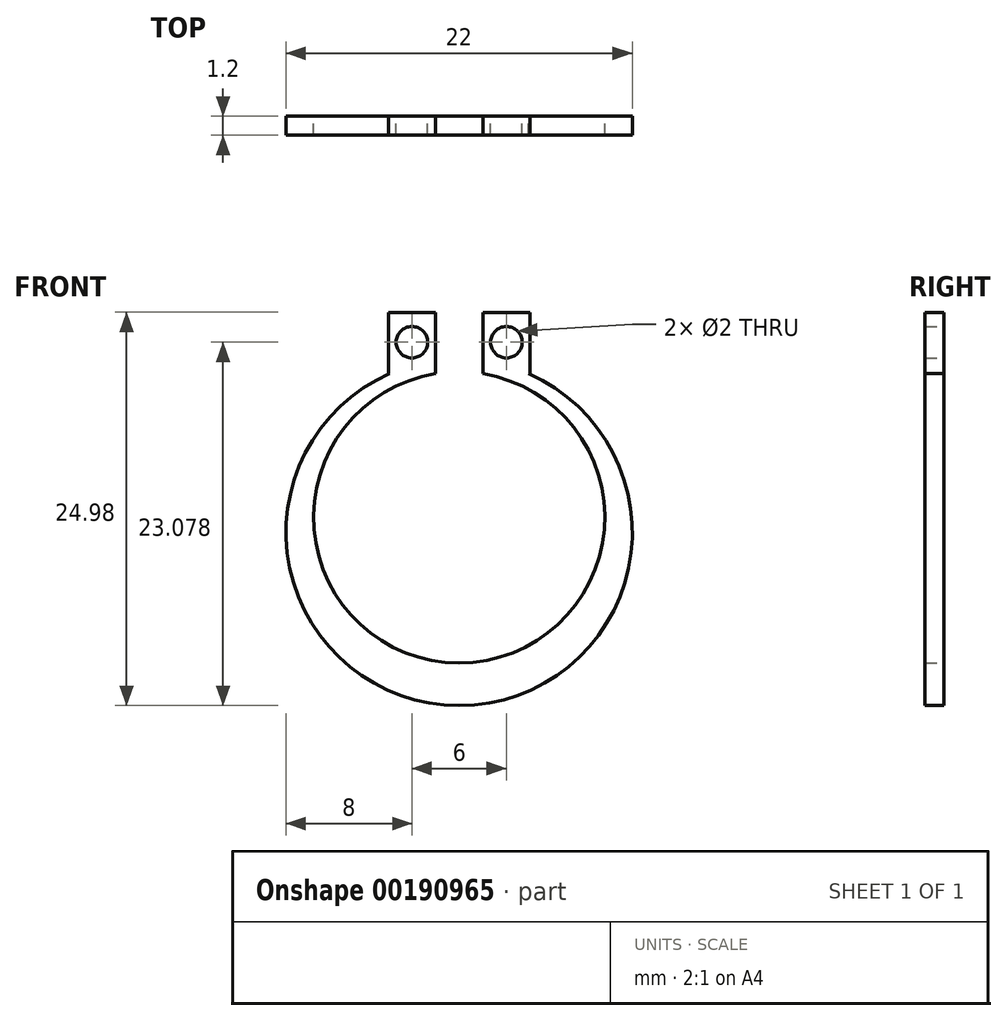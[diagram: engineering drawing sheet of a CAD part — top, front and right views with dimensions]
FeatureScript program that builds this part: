
annotation { "Feature Type Name" : "Feature", "Feature Type Description" : "" }
export const myFeature = defineFeature(function(context is Context, id is Id, definition is map)
    precondition{}
    {
        {
            var Q0;
            Q0=qCreatedBy(makeId("Front.planeOp"),FACE);
            var sketch = newSketch(context, id + "F0", { "sketchPlane" : qUnion([Q0])});
            skCircle(sketch, "E0", {"center": v(0, 0) * mm, "radius": 9.25 * mm});
            skCircle(sketch, "E1", {"center": v(0, -0.95) * mm, "radius": 11 * mm});
            skLineSegment(sketch, "E2.bottom", {"start": v(1.5, 9.13) * mm, "end": v(4.5, 9.13) * mm});
            skLineSegment(sketch, "E2.top", {"start": v(1.5, 13.03) * mm, "end": v(4.5, 13.03) * mm});
            skLineSegment(sketch, "E2.left", {"start": v(1.5, 9.13) * mm, "end": v(1.5, 13.03) * mm});
            skLineSegment(sketch, "E2.right", {"start": v(4.5, 9.13) * mm, "end": v(4.5, 13.03) * mm});
            skLineSegment(sketch, "E3.bottom", {"start": v(-1.5, 9.13) * mm, "end": v(-4.5, 9.13) * mm});
            skLineSegment(sketch, "E3.top", {"start": v(-1.5, 13.03) * mm, "end": v(-4.5, 13.03) * mm});
            skLineSegment(sketch, "E3.left", {"start": v(-1.5, 9.13) * mm, "end": v(-1.5, 13.03) * mm});
            skLineSegment(sketch, "E3.right", {"start": v(-4.5, 9.13) * mm, "end": v(-4.5, 13.03) * mm});
            skCircle(sketch, "E4", {"center": v(-3, 11.13) * mm, "radius": 1 * mm});
            skCircle(sketch, "E5", {"center": v(3, 11.13) * mm, "radius": 1 * mm});
            skSolve(sketch);
        }
        {
            var Q0;
            {var subQ0=sQuery(id+"F0.wireOp",EDGE,"E2.bottom");var subQ5=sQuery(id+"F0.wireOp",EDGE,"E1");var subQ6=makeQuery(id+"F0.imprint","INTERSECT",VERTEX,{"derivedFrom":[subQ5,subQ0]});Q0=makeQuery(id+"F0.imprint","IMPRINT",FACE,{"disambiguationData":[TD([[makeQuery(id+"F0.imprint","IMPRINT",EDGE,{"disambiguationData":[TD([[subQ6,1.0]])],"derivedFrom":subQ5}),1.0]])]});}
            var Q1;
            {var subQ1=sQuery(id+"F0.wireOp",EDGE,"E3.top");Q1=makeQuery(id+"F0.imprint","IMPRINT",FACE,{"disambiguationData":[TD([[makeQuery(id+"F0.imprint","IMPRINT",EDGE,{"derivedFrom":subQ1}),1.0]])]});}
            var Q2;
            {var subQ0=sQuery(id+"F0.wireOp",EDGE,"E3.left");var subQ1=sQuery(id+"F0.wireOp",EDGE,"E1");var subQ2=makeQuery(id+"F0.imprint","INTERSECT",VERTEX,{"derivedFrom":[subQ1,subQ0]});Q2=makeQuery(id+"F0.imprint","IMPRINT",FACE,{"disambiguationData":[TD([[makeQuery(id+"F0.imprint","IMPRINT",EDGE,{"disambiguationData":[TD([[subQ2,-1.0]])],"derivedFrom":subQ1}),1.0]])]});}
            var Q3;
            {var subQ1=sQuery(id+"F0.wireOp",EDGE,"E2.top");Q3=makeQuery(id+"F0.imprint","IMPRINT",FACE,{"disambiguationData":[TD([[makeQuery(id+"F0.imprint","IMPRINT",EDGE,{"derivedFrom":subQ1}),-1.0]])]});}
            var Q4;
            {var subQ0=sQuery(id+"F0.wireOp",EDGE,"E2.left");var subQ1=sQuery(id+"F0.wireOp",EDGE,"E1");var subQ2=makeQuery(id+"F0.imprint","INTERSECT",VERTEX,{"derivedFrom":[subQ1,subQ0]});Q4=makeQuery(id+"F0.imprint","IMPRINT",FACE,{"disambiguationData":[TD([[makeQuery(id+"F0.imprint","IMPRINT",EDGE,{"disambiguationData":[TD([[subQ2,1.0]])],"derivedFrom":subQ1}),1.0]])]});}
            extrude(context, id + "F1", {"entities" : qUnion([Q0, Q1, Q2, Q3, Q4]), "depth" : 1.2 * mm});
        }
    });
